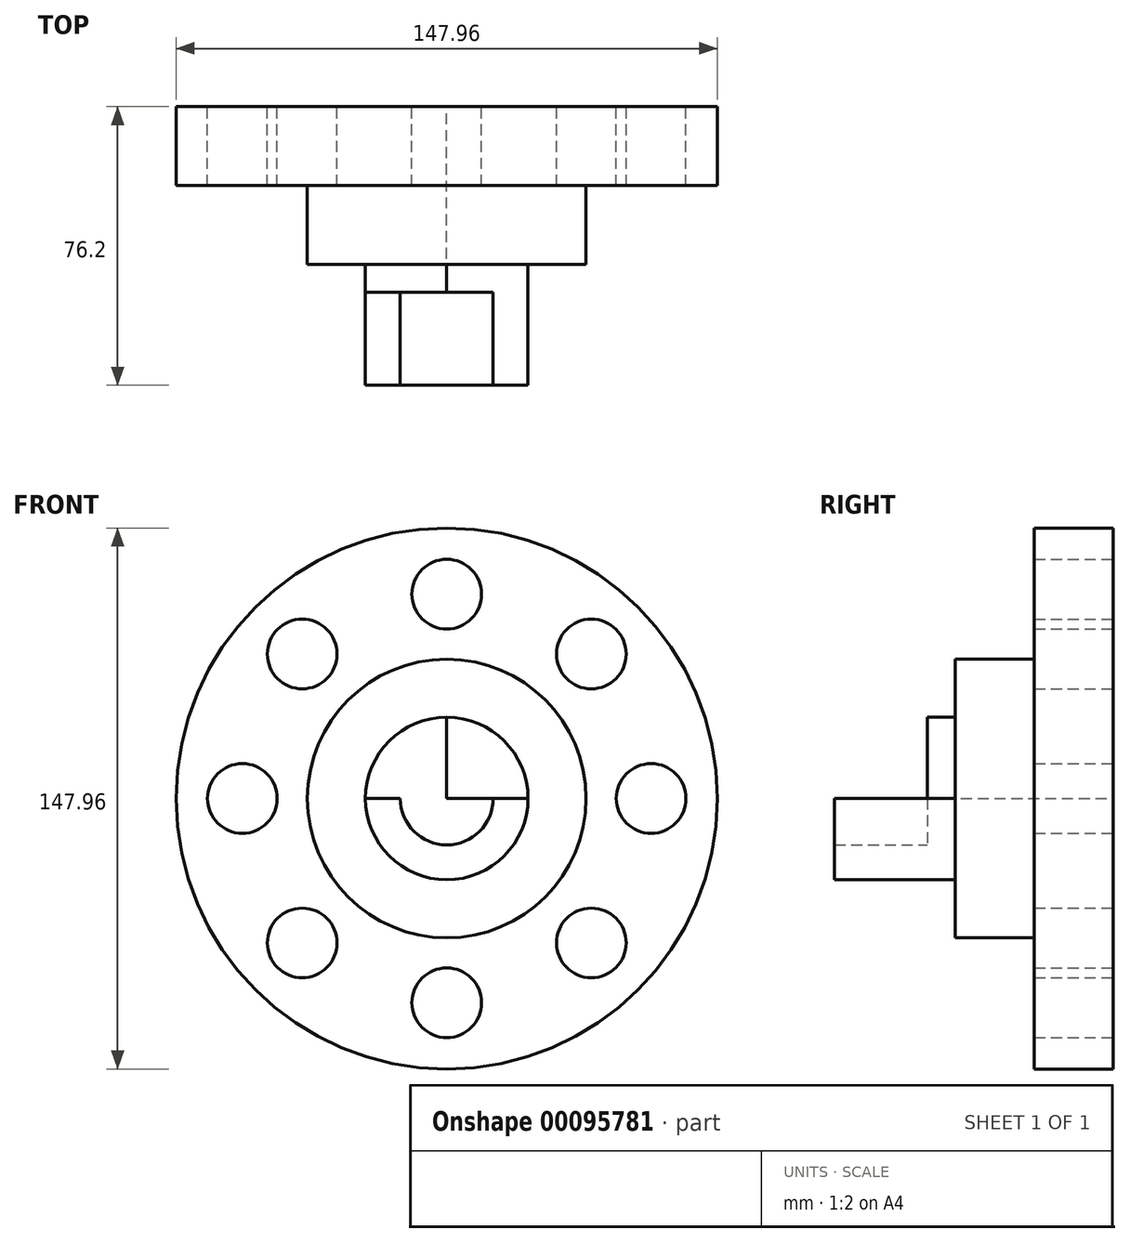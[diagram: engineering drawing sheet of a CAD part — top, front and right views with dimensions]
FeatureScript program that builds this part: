
annotation { "Feature Type Name" : "Feature", "Feature Type Description" : "" }
export const myFeature = defineFeature(function(context is Context, id is Id, definition is map)
    precondition{}
    {
        {
            var Q0;
            Q0=qCreatedBy(makeId("Front.planeOp"),FACE);
            var sketch = newSketch(context, id + "F0", { "sketchPlane" : qUnion([Q0])});
            skCircle(sketch, "E0", {"center": v(0, 0) * mm, "radius": 12.7 * mm});
            skCircle(sketch, "E1", {"center": v(0, 0) * mm, "radius": 22.23 * mm});
            skCircle(sketch, "E2", {"center": v(0, 0) * mm, "radius": 38.1 * mm});
            skCircle(sketch, "E3", {"center": v(0, 0) * mm, "radius": 55.88 * mm});
            skCircle(sketch, "E4", {"center": v(0, 0) * mm, "radius": 73.98 * mm});
            skCircle(sketch, "E5", {"center": v(0, 55.88) * mm, "radius": 9.53 * mm});
            skCircle(sketch, "E6.1.0", {"center": v(-39.51, 39.51) * mm, "radius": 9.53 * mm});
            skCircle(sketch, "E6.2.0", {"center": v(-55.88, 0) * mm, "radius": 9.53 * mm});
            skCircle(sketch, "E6.3.0", {"center": v(-39.51, -39.51) * mm, "radius": 9.53 * mm});
            skCircle(sketch, "E6.4.0", {"center": v(0, -55.88) * mm, "radius": 9.53 * mm});
            skCircle(sketch, "E6.5.0", {"center": v(39.51, -39.51) * mm, "radius": 9.53 * mm});
            skCircle(sketch, "E6.6.0", {"center": v(55.88, 0) * mm, "radius": 9.53 * mm});
            skCircle(sketch, "E6.7.0", {"center": v(39.51, 39.51) * mm, "radius": 9.53 * mm});
            skLineSegment(sketch, "E7", {"start": v(0, 55.88) * mm, "end": v(0, -55.88) * mm});
            skLineSegment(sketch, "E8", {"start": v(55.88, 0) * mm, "end": v(-55.88, 0) * mm});
            skLineSegment(sketch, "E9.bottom", {"start": v(3.17, -15.88) * mm, "end": v(-3.18, -15.88) * mm});
            skLineSegment(sketch, "E9.top", {"start": v(3.17, -9.53) * mm, "end": v(-3.18, -9.53) * mm});
            skLineSegment(sketch, "E9.left", {"start": v(3.17, -15.88) * mm, "end": v(3.17, -9.53) * mm});
            skLineSegment(sketch, "E9.right", {"start": v(-3.18, -15.88) * mm, "end": v(-3.18, -9.53) * mm});
            skPoint(sketch, "E9.middle", {"position": v(0, -12.7) * mm});
            skSolve(sketch);
        }
        {
            var Q0;
            Q0 = qSketchRegion(id + "F0", true);
            var Q1;
            Q1=makeQuery(id+"F0.imprint","IMPRINT",FACE,{"disambiguationData":[TD([[makeQuery(id+"F0.imprint","IMPRINT",EDGE,{"derivedFrom":sQuery(id+"F0.wireOp",EDGE,"E2")}),-1.0]])]});
            extrude(context, id + "F1", {"entities" : qUnion([Q0, Q1]), "depth" : 21.59 * mm});
        }
        {
            var Q0;
            {var subQ0=sQuery(id+"F0.wireOp",EDGE,"E7");var subQ1=sQuery(id+"F0.wireOp",EDGE,"E1");var subQ2=makeQuery(id+"F0.imprint","INTERSECT",VERTEX,{"disambiguationData":[OD(0.0)],"derivedFrom":[subQ1,subQ0]});Q0=makeQuery(id+"F0.imprint","IMPRINT",FACE,{"disambiguationData":[TD([[makeQuery(id+"F0.imprint","IMPRINT",EDGE,{"disambiguationData":[TD([[subQ2,-1.0]])],"derivedFrom":subQ1}),-1.0]])]});}
            var Q1;
            {var subQ0=sQuery(id+"F0.wireOp",EDGE,"E8");var subQ1=sQuery(id+"F0.wireOp",EDGE,"E1");var subQ2=makeQuery(id+"F0.imprint","INTERSECT",VERTEX,{"disambiguationData":[OD(1.0)],"derivedFrom":[subQ1,subQ0]});Q1=makeQuery(id+"F0.imprint","IMPRINT",FACE,{"disambiguationData":[TD([[makeQuery(id+"F0.imprint","IMPRINT",EDGE,{"disambiguationData":[TD([[subQ2,-1.0]])],"derivedFrom":subQ1}),-1.0]])]});}
            var Q2;
            {var subQ0=sQuery(id+"F0.wireOp",EDGE,"E8");var subQ1=sQuery(id+"F0.wireOp",EDGE,"E1");var subQ2=makeQuery(id+"F0.imprint","INTERSECT",VERTEX,{"disambiguationData":[OD(0.0)],"derivedFrom":[subQ1,subQ0]});Q2=makeQuery(id+"F0.imprint","IMPRINT",FACE,{"disambiguationData":[TD([[makeQuery(id+"F0.imprint","IMPRINT",EDGE,{"disambiguationData":[TD([[subQ2,1.0]])],"derivedFrom":subQ1}),-1.0]])]});}
            var Q3;
            {var subQ0=sQuery(id+"F0.wireOp",EDGE,"E7");var subQ1=sQuery(id+"F0.wireOp",EDGE,"E1");var subQ2=makeQuery(id+"F0.imprint","INTERSECT",VERTEX,{"disambiguationData":[OD(0.0)],"derivedFrom":[subQ1,subQ0]});Q3=makeQuery(id+"F0.imprint","IMPRINT",FACE,{"disambiguationData":[TD([[makeQuery(id+"F0.imprint","IMPRINT",EDGE,{"disambiguationData":[TD([[subQ2,1.0]])],"derivedFrom":subQ1}),-1.0]])]});}
            extrude(context, id + "F2", {"entities" : qUnion([Q0, Q1, Q2, Q3]), "operationType" : NewBodyOperationType.ADD, "depth" : 43.18 * mm});
        }
        {
            var Q0;
            {var subQ0=sQuery(id+"F0.wireOp",EDGE,"E7");var subQ1=sQuery(id+"F0.wireOp",EDGE,"E0");var subQ2=makeQuery(id+"F0.imprint","INTERSECT",VERTEX,{"disambiguationData":[OD(0.0)],"derivedFrom":[subQ1,subQ0]});Q0=makeQuery(id+"F0.imprint","IMPRINT",FACE,{"disambiguationData":[TD([[makeQuery(id+"F0.imprint","IMPRINT",EDGE,{"disambiguationData":[TD([[subQ2,-1.0]])],"derivedFrom":subQ1}),-1.0]])]});}
            var Q1;
            {var subQ0=sQuery(id+"F0.wireOp",EDGE,"E7");var subQ1=sQuery(id+"F0.wireOp",EDGE,"E0");var subQ2=makeQuery(id+"F0.imprint","INTERSECT",VERTEX,{"disambiguationData":[OD(0.0)],"derivedFrom":[subQ1,subQ0]});Q1=makeQuery(id+"F0.imprint","IMPRINT",FACE,{"disambiguationData":[TD([[makeQuery(id+"F0.imprint","IMPRINT",EDGE,{"disambiguationData":[TD([[subQ2,1.0]])],"derivedFrom":subQ1}),-1.0]])]});}
            var Q2;
            {var subQ0=sQuery(id+"F0.wireOp",EDGE,"E8");var subQ1=sQuery(id+"F0.wireOp",EDGE,"E0");var subQ2=makeQuery(id+"F0.imprint","INTERSECT",VERTEX,{"disambiguationData":[OD(0.0)],"derivedFrom":[subQ1,subQ0]});Q2=makeQuery(id+"F0.imprint","IMPRINT",FACE,{"disambiguationData":[TD([[makeQuery(id+"F0.imprint","IMPRINT",EDGE,{"disambiguationData":[TD([[subQ2,1.0]])],"derivedFrom":subQ1}),-1.0]])]});}
            var Q3;
            {var subQ0=sQuery(id+"F0.wireOp",EDGE,"E8");var subQ1=sQuery(id+"F0.wireOp",EDGE,"E0");var subQ2=makeQuery(id+"F0.imprint","INTERSECT",VERTEX,{"disambiguationData":[OD(1.0)],"derivedFrom":[subQ1,subQ0]});Q3=makeQuery(id+"F0.imprint","IMPRINT",FACE,{"disambiguationData":[TD([[makeQuery(id+"F0.imprint","IMPRINT",EDGE,{"disambiguationData":[TD([[subQ2,-1.0]])],"derivedFrom":subQ1}),-1.0]])]});}
            extrude(context, id + "F3", {"entities" : qUnion([Q0, Q1, Q2, Q3]), "operationType" : NewBodyOperationType.ADD, "depth" : 76.2 * mm});
        }
        {
            var Q0;
            {var subQ5=sQuery(id+"F0.wireOp",EDGE,"E8");var subQ6=sQuery(id+"F0.wireOp",EDGE,"E0");var subQ7=makeQuery(id+"F0.imprint","INTERSECT",VERTEX,{"disambiguationData":[OD(0.0)],"derivedFrom":[subQ6,subQ5]});Q0=makeQuery(id+"F0.imprint","IMPRINT",FACE,{"disambiguationData":[TD([[makeQuery(id+"F0.imprint","IMPRINT",EDGE,{"disambiguationData":[TD([[subQ7,1.0]])],"derivedFrom":subQ6}),1.0]])]});}
            var Q1;
            {var subQ5=sQuery(id+"F0.wireOp",EDGE,"E8");var subQ6=sQuery(id+"F0.wireOp",EDGE,"E0");var subQ7=makeQuery(id+"F0.imprint","INTERSECT",VERTEX,{"disambiguationData":[OD(1.0)],"derivedFrom":[subQ6,subQ5]});Q1=makeQuery(id+"F0.imprint","IMPRINT",FACE,{"disambiguationData":[TD([[makeQuery(id+"F0.imprint","IMPRINT",EDGE,{"disambiguationData":[TD([[subQ7,-1.0]])],"derivedFrom":subQ6}),1.0]])]});}
            var Q2;
            {var subQ0=sQuery(id+"F0.wireOp",EDGE,"E7");var subQ1=sQuery(id+"F0.wireOp",EDGE,"E0");var subQ2=makeQuery(id+"F0.imprint","INTERSECT",VERTEX,{"disambiguationData":[OD(0.0)],"derivedFrom":[subQ1,subQ0]});Q2=makeQuery(id+"F0.imprint","IMPRINT",FACE,{"disambiguationData":[TD([[makeQuery(id+"F0.imprint","IMPRINT",EDGE,{"disambiguationData":[TD([[subQ2,-1.0]])],"derivedFrom":subQ1}),1.0]])]});}
            var Q3;
            {var subQ0=sQuery(id+"F0.wireOp",EDGE,"E7");var subQ1=sQuery(id+"F0.wireOp",EDGE,"E0");var subQ2=makeQuery(id+"F0.imprint","INTERSECT",VERTEX,{"disambiguationData":[OD(0.0)],"derivedFrom":[subQ1,subQ0]});Q3=makeQuery(id+"F0.imprint","IMPRINT",FACE,{"disambiguationData":[TD([[makeQuery(id+"F0.imprint","IMPRINT",EDGE,{"disambiguationData":[TD([[subQ2,1.0]])],"derivedFrom":subQ1}),1.0]])]});}
            var Q4;
            {var subQ0=sQuery(id+"F0.wireOp",EDGE,"E9.right");var subQ1=sQuery(id+"F0.wireOp",EDGE,"E0");var subQ2=makeQuery(id+"F0.imprint","INTERSECT",VERTEX,{"derivedFrom":[subQ1,subQ0]});Q4=makeQuery(id+"F0.imprint","IMPRINT",FACE,{"disambiguationData":[TD([[makeQuery(id+"F0.imprint","IMPRINT",EDGE,{"disambiguationData":[TD([[subQ2,-1.0]])],"derivedFrom":subQ1}),-1.0]])]});}
            var Q5;
            {var subQ0=sQuery(id+"F0.wireOp",EDGE,"E7");var subQ1=sQuery(id+"F0.wireOp",EDGE,"E0");var subQ2=makeQuery(id+"F0.imprint","INTERSECT",VERTEX,{"disambiguationData":[OD(1.0)],"derivedFrom":[subQ1,subQ0]});Q5=makeQuery(id+"F0.imprint","IMPRINT",FACE,{"disambiguationData":[TD([[makeQuery(id+"F0.imprint","IMPRINT",EDGE,{"disambiguationData":[TD([[subQ2,-1.0]])],"derivedFrom":subQ1}),1.0]])]});}
            var Q6;
            {var subQ0=sQuery(id+"F0.wireOp",EDGE,"E7");var subQ1=sQuery(id+"F0.wireOp",EDGE,"E0");var subQ2=makeQuery(id+"F0.imprint","INTERSECT",VERTEX,{"disambiguationData":[OD(1.0)],"derivedFrom":[subQ1,subQ0]});Q6=makeQuery(id+"F0.imprint","IMPRINT",FACE,{"disambiguationData":[TD([[makeQuery(id+"F0.imprint","IMPRINT",EDGE,{"disambiguationData":[TD([[subQ2,-1.0]])],"derivedFrom":subQ1}),-1.0]])]});}
            var Q7;
            {var subQ0=sQuery(id+"F0.wireOp",EDGE,"E9.right");var subQ1=sQuery(id+"F0.wireOp",EDGE,"E0");var subQ2=makeQuery(id+"F0.imprint","INTERSECT",VERTEX,{"derivedFrom":[subQ1,subQ0]});Q7=makeQuery(id+"F0.imprint","IMPRINT",FACE,{"disambiguationData":[TD([[makeQuery(id+"F0.imprint","IMPRINT",EDGE,{"disambiguationData":[TD([[subQ2,-1.0]])],"derivedFrom":subQ1}),1.0]])]});}
            extrude(context, id + "F4", {"entities" : qUnion([Q0, Q1, Q2, Q3, Q4, Q5, Q6, Q7]), "operationType" : NewBodyOperationType.ADD, "depth" : 50.8 * mm});
        }
    });
